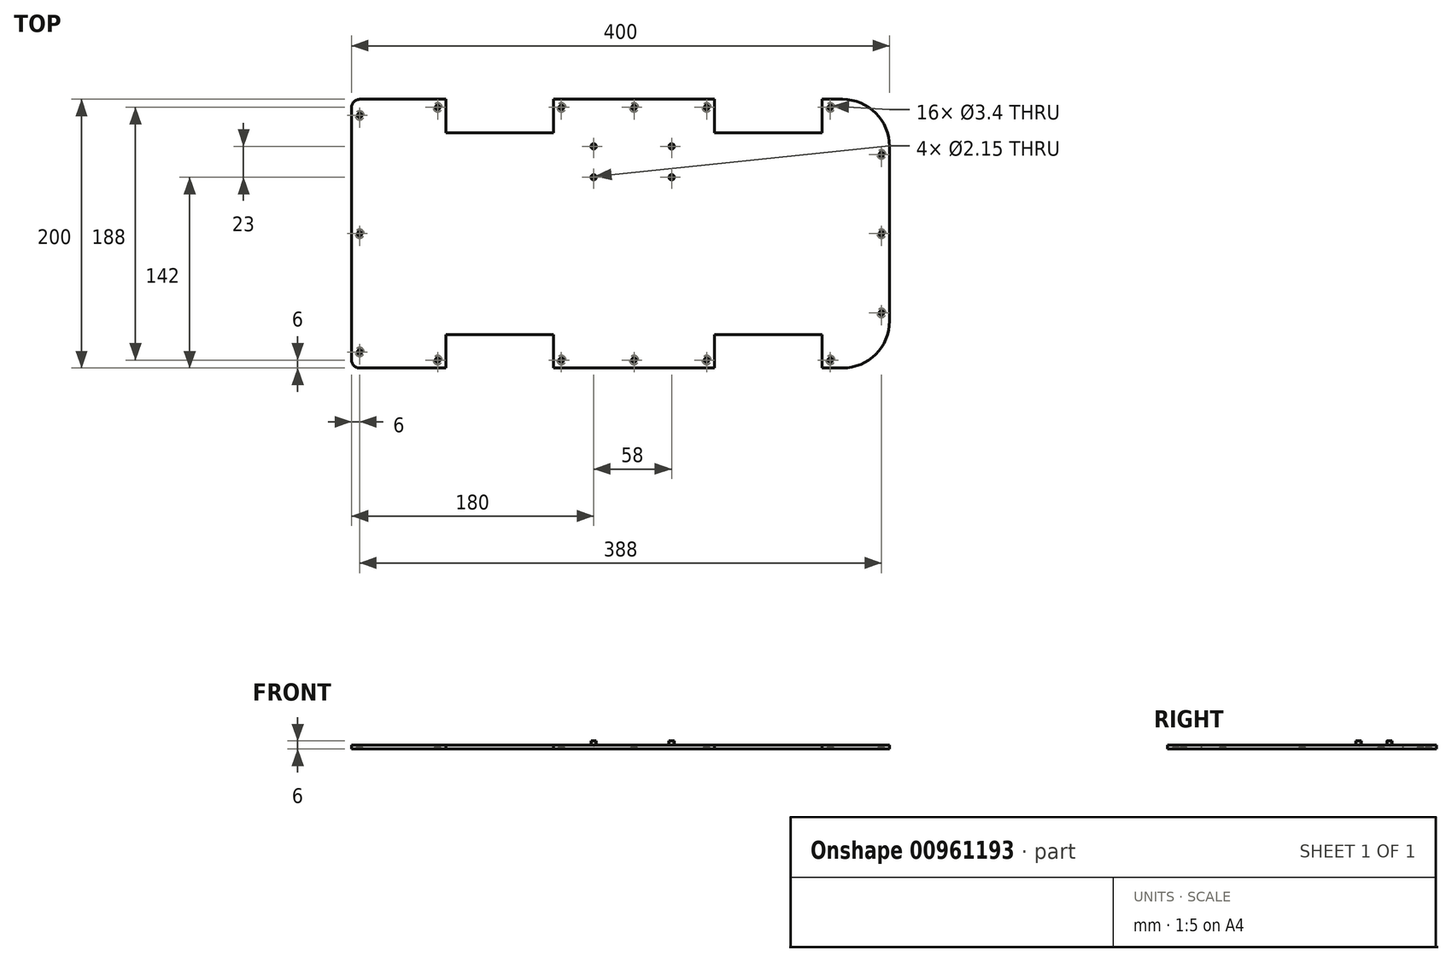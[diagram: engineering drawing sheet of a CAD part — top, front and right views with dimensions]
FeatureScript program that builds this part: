
annotation { "Feature Type Name" : "Feature", "Feature Type Description" : "" }
export const myFeature = defineFeature(function(context is Context, id is Id, definition is map)
    precondition{}
    {
        {
            var Q0;
            Q0=qCreatedBy(makeId("Top.planeOp"),FACE);
            var sketch = newSketch(context, id + "F0", { "sketchPlane" : qUnion([Q0])});
            skLineSegment(sketch, "E0.bottom", {"start": v(-194, 100) * mm, "end": v(-130, 100) * mm});
            skLineSegment(sketch, "E0.left", {"start": v(-200, 94) * mm, "end": v(-200, 0) * mm});
            skLineSegment(sketch, "E0.right", {"start": v(200, 65) * mm, "end": v(200, 0) * mm});
            skLineSegment(sketch, "E1.top", {"start": v(70, 75) * mm, "end": v(150, 75) * mm});
            skLineSegment(sketch, "E1.left", {"start": v(70, 100) * mm, "end": v(70, 75) * mm});
            skLineSegment(sketch, "E1.right", {"start": v(150, 100) * mm, "end": v(150, 75) * mm});
            skLineSegment(sketch, "E2.trimOffspring", {"start": v(150, 100) * mm, "end": v(165, 100) * mm});
            skLineSegment(sketch, "E3.top", {"start": v(-130, 75) * mm, "end": v(-50, 75) * mm});
            skLineSegment(sketch, "E3.left", {"start": v(-130, 100) * mm, "end": v(-130, 75) * mm});
            skLineSegment(sketch, "E3.right", {"start": v(-50, 100) * mm, "end": v(-50, 75) * mm});
            skLineSegment(sketch, "E4.trimOffspring", {"start": v(-50, 100) * mm, "end": v(70, 100) * mm});
            skPoint(sketch, "E5.orphan", {"position": v(200, 0) * mm});
            skPoint(sketch, "E6.orphan", {"position": v(-200, 0) * mm});
            skArc(sketch, "E7.filletArc", {"start": v(200, 65) * mm, "mid": v(189.75, 89.75) * mm, "end": v(165, 100) * mm});
            skArc(sketch, "E8.filletArc", {"start": v(-194, 100) * mm, "mid": v(-198.24, 98.24) * mm, "end": v(-200, 94) * mm});
            skLineSegment(sketch, "E9", {"start": v(-219.97, 0) * mm, "end": v(220.1, 0) * mm, "construction": true});
            skLineSegment(sketch, "E10", {"start": v(-90, 116.05) * mm, "end": v(-90, -112.48) * mm, "construction": true});
            skPoint(sketch, "E10.startSnap0", {"position": v(-90, 75) * mm});
            skLineSegment(sketch, "E11", {"start": v(110, 116.05) * mm, "end": v(110, -118.3) * mm, "construction": true});
            skPoint(sketch, "E11.startSnap0", {"position": v(110, 75) * mm});
            skLineSegment(sketch, "E12.MirrorCS", {"start": v(-194, -100) * mm, "end": v(-130, -100) * mm});
            skLineSegment(sketch, "E13.MirrorCS", {"start": v(200, -65) * mm, "end": v(200, 0) * mm});
            skLineSegment(sketch, "E14.MirrorCS", {"start": v(-130, -75) * mm, "end": v(-50, -75) * mm});
            skPoint(sketch, "E15.MirrorP", {"position": v(110, -75) * mm});
            skLineSegment(sketch, "E16.MirrorCS", {"start": v(-50, -100) * mm, "end": v(-50, -75) * mm});
            skArc(sketch, "E17.MirrorCS", {"start": v(200, -65) * mm, "mid": v(189.75, -89.75) * mm, "end": v(165, -100) * mm});
            skLineSegment(sketch, "E18.MirrorCS", {"start": v(-50, -100) * mm, "end": v(70, -100) * mm});
            skLineSegment(sketch, "E19.MirrorCS", {"start": v(150, -100) * mm, "end": v(150, -75) * mm});
            skLineSegment(sketch, "E20.MirrorCS", {"start": v(-200, -94) * mm, "end": v(-200, 0) * mm});
            skLineSegment(sketch, "E21.MirrorCS", {"start": v(70, -75) * mm, "end": v(150, -75) * mm});
            skLineSegment(sketch, "E22.MirrorCS", {"start": v(-130, -100) * mm, "end": v(-130, -75) * mm});
            skLineSegment(sketch, "E23.MirrorCS", {"start": v(150, -100) * mm, "end": v(165, -100) * mm});
            skLineSegment(sketch, "E24.MirrorCS", {"start": v(70, -100) * mm, "end": v(70, -75) * mm});
            skArc(sketch, "E25.MirrorCS", {"start": v(-194, -100) * mm, "mid": v(-198.24, -98.24) * mm, "end": v(-200, -94) * mm});
            skPoint(sketch, "E26.MirrorP", {"position": v(-90, -75) * mm});
            skSolve(sketch);
        }
        {
            var Q0;
            Q0 = qSketchRegion(id + "F0", true);
            extrude(context, id + "F1", {"entities" : qUnion([Q0]), "depth" : 3 * mm, "offsetDistance" : 25 * mm});
        }
        {
            var Q0;
            Q0=makeQuery(id+"F1.opExtrude","CAP_FACE",FACE,{"disambiguationData":[OSD([sQuery(id+"F0.wireOp",EDGE,"E0.bottom"),sQuery(id+"F0.wireOp",EDGE,"E0.left"),sQuery(id+"F0.wireOp",EDGE,"E0.right"),sQuery(id+"F0.wireOp",EDGE,"E1.top"),sQuery(id+"F0.wireOp",EDGE,"E1.left"),sQuery(id+"F0.wireOp",EDGE,"E1.right"),sQuery(id+"F0.wireOp",EDGE,"E2.trimOffspring"),sQuery(id+"F0.wireOp",EDGE,"E3.top"),sQuery(id+"F0.wireOp",EDGE,"E3.left"),sQuery(id+"F0.wireOp",EDGE,"E3.right"),sQuery(id+"F0.wireOp",EDGE,"E4.trimOffspring"),sQuery(id+"F0.wireOp",EDGE,"E7.filletArc"),sQuery(id+"F0.wireOp",EDGE,"E8.filletArc"),sQuery(id+"F0.wireOp",EDGE,"E12.MirrorCS"),sQuery(id+"F0.wireOp",EDGE,"E13.MirrorCS"),sQuery(id+"F0.wireOp",EDGE,"E14.MirrorCS"),sQuery(id+"F0.wireOp",EDGE,"E16.MirrorCS"),sQuery(id+"F0.wireOp",EDGE,"E17.MirrorCS"),sQuery(id+"F0.wireOp",EDGE,"E18.MirrorCS"),sQuery(id+"F0.wireOp",EDGE,"E19.MirrorCS"),sQuery(id+"F0.wireOp",EDGE,"E20.MirrorCS"),sQuery(id+"F0.wireOp",EDGE,"E21.MirrorCS"),sQuery(id+"F0.wireOp",EDGE,"E22.MirrorCS"),sQuery(id+"F0.wireOp",EDGE,"E23.MirrorCS"),sQuery(id+"F0.wireOp",EDGE,"E24.MirrorCS"),sQuery(id+"F0.wireOp",EDGE,"E25.MirrorCS")])],"isStart":false});
            var sketch = newSketch(context, id + "F2", { "sketchPlane" : qUnion([Q0])});
            skLineSegment(sketch, "E27.bottom", {"start": v(-20, 65) * mm, "end": v(38, 65) * mm, "construction": true});
            skLineSegment(sketch, "E27.top", {"start": v(-20, 42) * mm, "end": v(38, 42) * mm, "construction": true});
            skLineSegment(sketch, "E27.left", {"start": v(-20, 65) * mm, "end": v(-20, 42) * mm, "construction": true});
            skLineSegment(sketch, "E27.right", {"start": v(38, 65) * mm, "end": v(38, 42) * mm, "construction": true});
            skCircle(sketch, "E28", {"center": v(-20, 65) * mm, "radius": 2 * mm});
            skCircle(sketch, "E29.0.1.0", {"center": v(-20, 42) * mm, "radius": 2 * mm});
            skCircle(sketch, "E29.1.0.0", {"center": v(38, 65) * mm, "radius": 2 * mm});
            skCircle(sketch, "E29.1.1.0", {"center": v(38, 42) * mm, "radius": 2 * mm});
            skSolve(sketch);
        }
        {
            var Q0;
            Q0=makeQuery(id+"F2.imprint","IMPRINT",FACE,{"disambiguationData":[TD([[makeQuery(id+"F2.imprint","IMPRINT",EDGE,{"derivedFrom":sQuery(id+"F2.wireOp",EDGE,"E29.1.1.0")}),1.0]])]});
            var Q1;
            Q1=makeQuery(id+"F2.imprint","IMPRINT",FACE,{"disambiguationData":[TD([[makeQuery(id+"F2.imprint","IMPRINT",EDGE,{"derivedFrom":sQuery(id+"F2.wireOp",EDGE,"E29.1.0.0")}),1.0]])]});
            var Q2;
            Q2=makeQuery(id+"F2.imprint","IMPRINT",FACE,{"disambiguationData":[TD([[makeQuery(id+"F2.imprint","IMPRINT",EDGE,{"derivedFrom":sQuery(id+"F2.wireOp",EDGE,"E29.0.1.0")}),1.0]])]});
            var Q3;
            Q3=makeQuery(id+"F2.imprint","IMPRINT",FACE,{"disambiguationData":[TD([[makeQuery(id+"F2.imprint","IMPRINT",EDGE,{"derivedFrom":sQuery(id+"F2.wireOp",EDGE,"E28")}),1.0]])]});
            extrude(context, id + "F3", {"entities" : qUnion([Q0, Q1, Q2, Q3]), "operationType" : NewBodyOperationType.ADD, "depth" : 3 * mm, "offsetDistance" : 25 * mm});
        }
        {
            var Q0;
            Q0=makeQuery(id+"F3.opExtrude","CAP_FACE",FACE,{"disambiguationData":[OSD([sQuery(id+"F2.wireOp",EDGE,"E29.1.1.0")])],"isStart":false});
            var sketch = newSketch(context, id + "F4", { "sketchPlane" : qUnion([Q0])});
            skPoint(sketch, "E30", {"position": v(38, 42) * mm});
            skPoint(sketch, "E31", {"position": v(38, 65) * mm});
            skPoint(sketch, "E32", {"position": v(-20, 65) * mm});
            skPoint(sketch, "E33", {"position": v(-20, 42) * mm});
            skSolve(sketch);
        }
        {
            var Q0;
            Q0=sQuery(id+"F4.wireOp",VERTEX,"E33");
            var Q1;
            Q1=sQuery(id+"F4.wireOp",VERTEX,"E32");
            var Q2;
            Q2=sQuery(id+"F4.wireOp",VERTEX,"E31");
            var Q3;
            Q3=sQuery(id+"F4.wireOp",VERTEX,"E30");
            var Q4;
            Q4=makeQuery(id+"F1.opExtrude","SWEPT_BODY",BODY,{"disambiguationData":[OSD([sQuery(id+"F0.wireOp",EDGE,"E0.bottom"),sQuery(id+"F0.wireOp",EDGE,"E0.left"),sQuery(id+"F0.wireOp",EDGE,"E0.right"),sQuery(id+"F0.wireOp",EDGE,"E1.top"),sQuery(id+"F0.wireOp",EDGE,"E1.left"),sQuery(id+"F0.wireOp",EDGE,"E1.right"),sQuery(id+"F0.wireOp",EDGE,"E2.trimOffspring"),sQuery(id+"F0.wireOp",EDGE,"E3.top"),sQuery(id+"F0.wireOp",EDGE,"E3.left"),sQuery(id+"F0.wireOp",EDGE,"E3.right"),sQuery(id+"F0.wireOp",EDGE,"E4.trimOffspring"),sQuery(id+"F0.wireOp",EDGE,"E7.filletArc"),sQuery(id+"F0.wireOp",EDGE,"E8.filletArc"),sQuery(id+"F0.wireOp",EDGE,"E12.MirrorCS"),sQuery(id+"F0.wireOp",EDGE,"E13.MirrorCS"),sQuery(id+"F0.wireOp",EDGE,"E14.MirrorCS"),sQuery(id+"F0.wireOp",EDGE,"E16.MirrorCS"),sQuery(id+"F0.wireOp",EDGE,"E17.MirrorCS"),sQuery(id+"F0.wireOp",EDGE,"E18.MirrorCS"),sQuery(id+"F0.wireOp",EDGE,"E19.MirrorCS"),sQuery(id+"F0.wireOp",EDGE,"E20.MirrorCS"),sQuery(id+"F0.wireOp",EDGE,"E21.MirrorCS"),sQuery(id+"F0.wireOp",EDGE,"E22.MirrorCS"),sQuery(id+"F0.wireOp",EDGE,"E23.MirrorCS"),sQuery(id+"F0.wireOp",EDGE,"E24.MirrorCS"),sQuery(id+"F0.wireOp",EDGE,"E25.MirrorCS")])]});
            hole(context, id + "F5", {"style" : HoleStyle.SIMPLE, "endStyle" : HoleEndStyle.BLIND, "standardTappedOrClearance" : lookupTablePath({ "standard" : "ISO", "engagement" : "75%", "pitch" : "0.35 mm", "size" : "M2.5", "type" : "Tapped" }), "standardBlindInLast" : lookupTablePath({ "standard" : "ISO", "fit" : "Normal", "engagement" : "75%", "pitch" : "0.35 mm", "size" : "M2.5", "type" : "Clearance & tapped" }), "holeDiameter" : 2.15 * mm, "majorDiameter" : 2.5 * mm, "showTappedDepth" : true, "holeDepth" : 3 * mm, "isTappedThrough" : true, "tappedDepth" : 2.83 * mm, "tapClearance" : 0.5, "locations" : qUnion([Q0, Q1, Q2, Q3]), "scope" : qUnion([Q4])});
        }
        {
            var Q0;
            Q0=makeQuery(id+"F1.opExtrude","CAP_FACE",FACE,{"disambiguationData":[OSD([sQuery(id+"F0.wireOp",EDGE,"E0.bottom"),sQuery(id+"F0.wireOp",EDGE,"E0.left"),sQuery(id+"F0.wireOp",EDGE,"E0.right"),sQuery(id+"F0.wireOp",EDGE,"E1.top"),sQuery(id+"F0.wireOp",EDGE,"E1.left"),sQuery(id+"F0.wireOp",EDGE,"E1.right"),sQuery(id+"F0.wireOp",EDGE,"E2.trimOffspring"),sQuery(id+"F0.wireOp",EDGE,"E3.top"),sQuery(id+"F0.wireOp",EDGE,"E3.left"),sQuery(id+"F0.wireOp",EDGE,"E3.right"),sQuery(id+"F0.wireOp",EDGE,"E4.trimOffspring"),sQuery(id+"F0.wireOp",EDGE,"E7.filletArc"),sQuery(id+"F0.wireOp",EDGE,"E8.filletArc"),sQuery(id+"F0.wireOp",EDGE,"E12.MirrorCS"),sQuery(id+"F0.wireOp",EDGE,"E13.MirrorCS"),sQuery(id+"F0.wireOp",EDGE,"E14.MirrorCS"),sQuery(id+"F0.wireOp",EDGE,"E16.MirrorCS"),sQuery(id+"F0.wireOp",EDGE,"E17.MirrorCS"),sQuery(id+"F0.wireOp",EDGE,"E18.MirrorCS"),sQuery(id+"F0.wireOp",EDGE,"E19.MirrorCS"),sQuery(id+"F0.wireOp",EDGE,"E20.MirrorCS"),sQuery(id+"F0.wireOp",EDGE,"E21.MirrorCS"),sQuery(id+"F0.wireOp",EDGE,"E22.MirrorCS"),sQuery(id+"F0.wireOp",EDGE,"E23.MirrorCS"),sQuery(id+"F0.wireOp",EDGE,"E24.MirrorCS"),sQuery(id+"F0.wireOp",EDGE,"E25.MirrorCS")])],"isStart":true});
            var sketch = newSketch(context, id + "F6", { "sketchPlane" : qUnion([Q0])});
            skPoint(sketch, "E34", {"position": v(-136, 94) * mm});
            skPoint(sketch, "E35", {"position": v(-194, 88) * mm});
            skPoint(sketch, "E36", {"position": v(-194, -88) * mm});
            skPoint(sketch, "E37", {"position": v(-136, -94) * mm});
            skPoint(sketch, "E37.positionSnap0", {"position": v(-136, -100.32) * mm});
            skPoint(sketch, "E38", {"position": v(-44, -94) * mm});
            skPoint(sketch, "E39", {"position": v(10, -94) * mm});
            skPoint(sketch, "E39.positionSnap0", {"position": v(10, -100) * mm});
            skPoint(sketch, "E40", {"position": v(64, -94) * mm});
            skPoint(sketch, "E41", {"position": v(156, -94) * mm});
            skPoint(sketch, "E42", {"position": v(194, -59) * mm});
            skPoint(sketch, "E43", {"position": v(194, 0) * mm});
            skPoint(sketch, "E43.positionSnap0", {"position": v(200, 0) * mm});
            skPoint(sketch, "E44", {"position": v(194, 59) * mm});
            skPoint(sketch, "E45", {"position": v(156, 94) * mm});
            skPoint(sketch, "E46", {"position": v(64, 94) * mm});
            skPoint(sketch, "E47", {"position": v(10, 94) * mm});
            skPoint(sketch, "E47.positionSnap0", {"position": v(10, 100) * mm});
            skPoint(sketch, "E48", {"position": v(-44, 94) * mm});
            skPoint(sketch, "E49", {"position": v(-194, 0) * mm});
            skPoint(sketch, "E49.positionSnap0", {"position": v(-200, 0) * mm});
            skSolve(sketch);
        }
        {
            var Q0;
            Q0=sQuery(id+"F6.wireOp",VERTEX,"E37");
            var Q1;
            Q1=sQuery(id+"F6.wireOp",VERTEX,"E36");
            var Q2;
            Q2=sQuery(id+"F6.wireOp",VERTEX,"E35");
            var Q3;
            Q3=sQuery(id+"F6.wireOp",VERTEX,"E34");
            var Q4;
            Q4=sQuery(id+"F6.wireOp",VERTEX,"E48");
            var Q5;
            Q5=sQuery(id+"F6.wireOp",VERTEX,"E47");
            var Q6;
            Q6=sQuery(id+"F6.wireOp",VERTEX,"E46");
            var Q7;
            Q7=sQuery(id+"F6.wireOp",VERTEX,"E45");
            var Q8;
            Q8=sQuery(id+"F6.wireOp",VERTEX,"E44");
            var Q9;
            Q9=sQuery(id+"F6.wireOp",VERTEX,"E43");
            var Q10;
            Q10=sQuery(id+"F6.wireOp",VERTEX,"E42");
            var Q11;
            Q11=sQuery(id+"F6.wireOp",VERTEX,"E41");
            var Q12;
            Q12=sQuery(id+"F6.wireOp",VERTEX,"E40");
            var Q13;
            Q13=sQuery(id+"F6.wireOp",VERTEX,"E39");
            var Q14;
            Q14=sQuery(id+"F6.wireOp",VERTEX,"E38");
            var Q15;
            Q15=sQuery(id+"F6.wireOp",VERTEX,"E49");
            var Q16;
            Q16=makeQuery(id+"F1.opExtrude","SWEPT_BODY",BODY,{"disambiguationData":[OSD([sQuery(id+"F0.wireOp",EDGE,"E0.bottom"),sQuery(id+"F0.wireOp",EDGE,"E0.left"),sQuery(id+"F0.wireOp",EDGE,"E0.right"),sQuery(id+"F0.wireOp",EDGE,"E1.top"),sQuery(id+"F0.wireOp",EDGE,"E1.left"),sQuery(id+"F0.wireOp",EDGE,"E1.right"),sQuery(id+"F0.wireOp",EDGE,"E2.trimOffspring"),sQuery(id+"F0.wireOp",EDGE,"E3.top"),sQuery(id+"F0.wireOp",EDGE,"E3.left"),sQuery(id+"F0.wireOp",EDGE,"E3.right"),sQuery(id+"F0.wireOp",EDGE,"E4.trimOffspring"),sQuery(id+"F0.wireOp",EDGE,"E7.filletArc"),sQuery(id+"F0.wireOp",EDGE,"E8.filletArc"),sQuery(id+"F0.wireOp",EDGE,"E12.MirrorCS"),sQuery(id+"F0.wireOp",EDGE,"E13.MirrorCS"),sQuery(id+"F0.wireOp",EDGE,"E14.MirrorCS"),sQuery(id+"F0.wireOp",EDGE,"E16.MirrorCS"),sQuery(id+"F0.wireOp",EDGE,"E17.MirrorCS"),sQuery(id+"F0.wireOp",EDGE,"E18.MirrorCS"),sQuery(id+"F0.wireOp",EDGE,"E19.MirrorCS"),sQuery(id+"F0.wireOp",EDGE,"E20.MirrorCS"),sQuery(id+"F0.wireOp",EDGE,"E21.MirrorCS"),sQuery(id+"F0.wireOp",EDGE,"E22.MirrorCS"),sQuery(id+"F0.wireOp",EDGE,"E23.MirrorCS"),sQuery(id+"F0.wireOp",EDGE,"E24.MirrorCS"),sQuery(id+"F0.wireOp",EDGE,"E25.MirrorCS")])]});
            hole(context, id + "F7", {"style" : HoleStyle.C_SINK, "endStyle" : HoleEndStyle.THROUGH, "standardTappedOrClearance" : lookupTablePath({ "fit" : "Normal", "standard" : "ISO", "size" : "M3", "type" : "Clearance" }), "standardBlindInLast" : lookupTablePath({ "fit" : "Normal", "standard" : "ISO", "engagement" : "75%", "pitch" : "0.5 mm", "size" : "M3", "type" : "Clearance & tapped" }), "holeDiameter" : 3.4 * mm, "cSinkDiameter" : 6.72 * mm, "cSinkAngle" : 90 * degree, "majorDiameter" : 5 * mm, "isTappedThrough" : true, "tappedDepth" : 1.95 * mm, "tapClearance" : 3, "locations" : qUnion([Q0, Q1, Q2, Q3, Q4, Q5, Q6, Q7, Q8, Q9, Q10, Q11, Q12, Q13, Q14, Q15]), "scope" : qUnion([Q16])});
        }
    });
